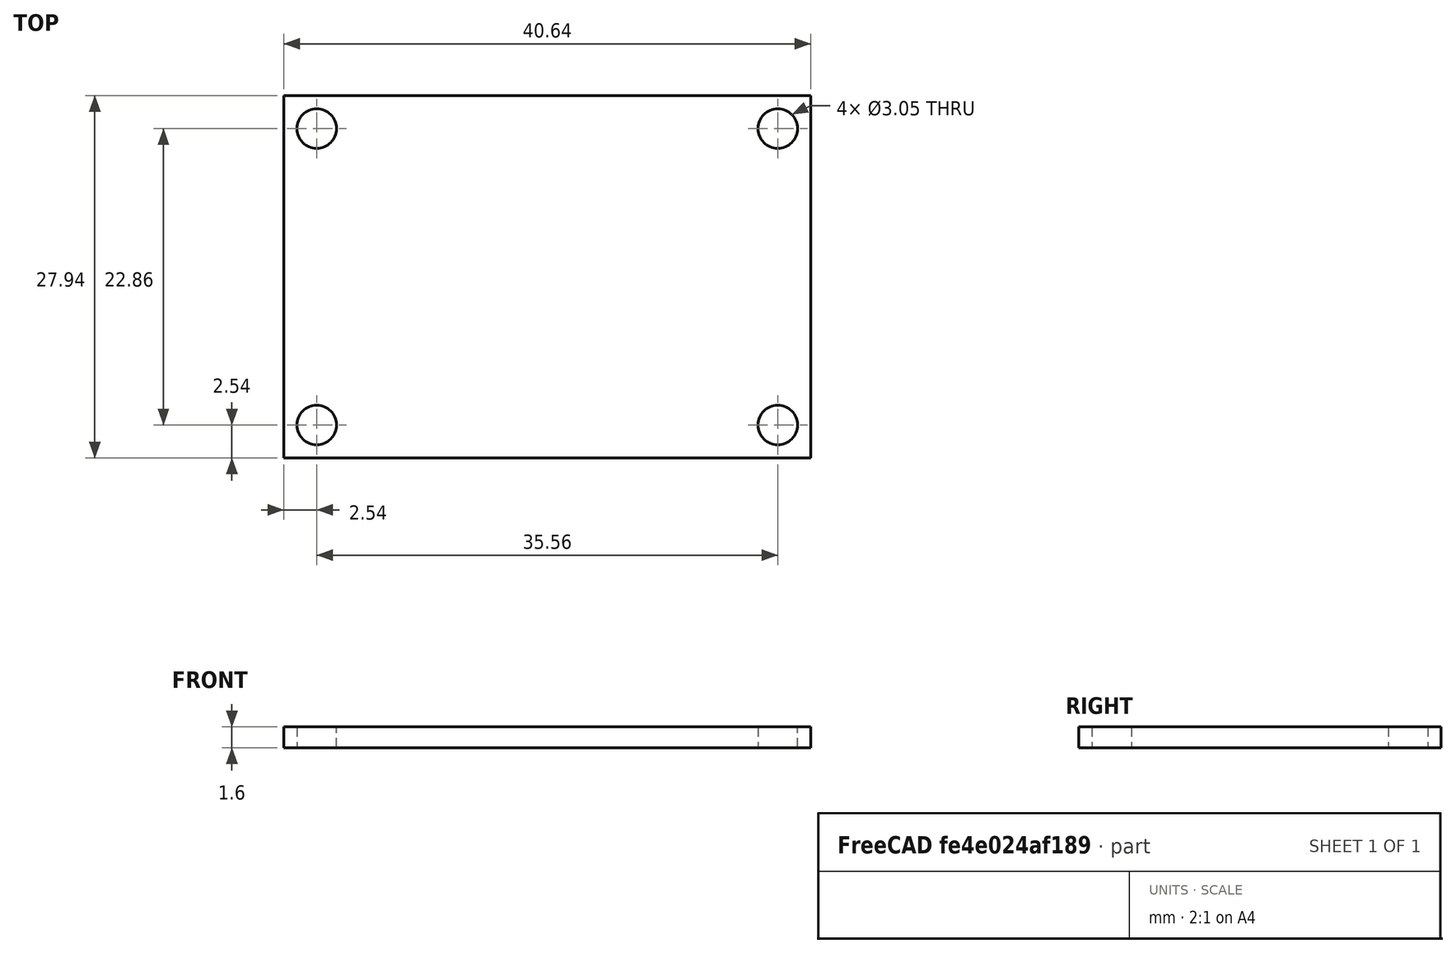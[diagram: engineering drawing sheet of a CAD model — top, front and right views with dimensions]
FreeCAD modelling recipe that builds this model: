
FCSTD DOCUMENT  (FreeCAD 0.21R33668 +26 (Git))
Label: Alphanumeric_Dimensional_Mounting
License: All rights reserved
LicenseURL: http://en.wikipedia.org/wiki/All_rights_reserved
objects: Sketcher::SketchObject×1, PartDesign::Pad×1, PartDesign::Body×1
note: 4 computed .brp shape members not serialized (recipe doc carries the construction recipe); baked Part::Feature solids carry a one-line shape summary decoded from their .brp

FEATURE [Sketcher::SketchObject] Sketch
  FullyConstrained = true
  MapMode = 5
  Support = -> [XY_Plane]
  sketch-geometry (8):
    g0: LineSegment StartX=-20.32 StartY=13.97 StartZ=0 EndX=20.32 EndY=13.97 EndZ=0
    g1: LineSegment StartX=20.32 StartY=13.97 StartZ=0 EndX=20.32 EndY=-13.97 EndZ=0
    g2: LineSegment StartX=20.32 StartY=-13.97 StartZ=0 EndX=-20.32 EndY=-13.97 EndZ=0
    g3: LineSegment StartX=-20.32 StartY=-13.97 StartZ=0 EndX=-20.32 EndY=13.97 EndZ=0
    g4: Circle CenterX=-17.78 CenterY=11.43 CenterZ=0 NormalX=0 NormalY=0 NormalZ=1 AngleXU=0 Radius=1.524
    g5: Circle CenterX=-17.78 CenterY=-11.43 CenterZ=0 NormalX=0 NormalY=0 NormalZ=1 AngleXU=0 Radius=1.524
    g6: Circle CenterX=17.78 CenterY=-11.43 CenterZ=0 NormalX=0 NormalY=0 NormalZ=1 AngleXU=0 Radius=1.524
    g7: Circle CenterX=17.78 CenterY=11.43 CenterZ=0 NormalX=0 NormalY=0 NormalZ=1 AngleXU=0 Radius=1.524
  constraints (21):
    c: Coincident(g0,g1)
    c: Coincident(g1,g2)
    c: Coincident(g2,g3)
    c: Coincident(g3,g0)
    c: Horizontal(g0)
    c: Horizontal(g2)
    c: Vertical(g1)
    c: Vertical(g3)
    c: DistanceY(g1,g1) = 27.94
    c: DistanceX(g0,g0) = 40.64
    c: Symmetric(g1,g0,g-1)
    c: Diameter(g4) = 3.048
    c: Equal(g4,g7)
    c: Equal(g4,g5)
    c: Equal(g4,g6)
    c: DistanceX(g4,g7) = 35.56
    c: Vertical(g7,g6)
    c: DistanceY(g5,g4) = 22.86
    c: Symmetric(g7,g4,g-2)
    c: Horizontal(g6,g5)
    c: Symmetric(g4,g5,g-1)
FEATURE [PartDesign::Pad] Pad
  Direction = (0,0,1)
  Length = 1.6
  Length2 = 10
  Profile = -> Sketch
  ReferenceAxis = -> Sketch [N_Axis]
  Type = 0
FEATURE [PartDesign::Body] Body
  Group = -> [Sketch,Pad]
  Origin = -> Origin
  Tip = -> Pad
